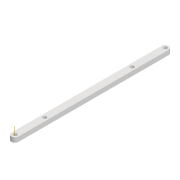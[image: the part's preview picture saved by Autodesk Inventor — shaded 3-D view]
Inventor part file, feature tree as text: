
AUTODESK INVENTOR PART (.ipt)
format: ipt  version: 2022 (Build 260153000, 153)  size: 93,696 bytes
history: native  units: mm
features: extrude x1, other x1, sketch x1
ambient origin geometry x8: Origin, YZ Plane, XZ Plane, XY Plane, X Axis, Y Axis, Z Axis, Center Point
bodies: Solid1 (feature_tree)
feature tree (3):
  extrude  "Extrusion1"  Depth=101.165mm
  other  "Work Axis2"
  sketch  "Sketch1"  dims[d0=3.2mm d1=3.2mm d2=6.0mm d3=129.784mm d4=3.2mm d5=25.613mm d6=4.0mm d7=0.0mm d8=3.2mm d9=101.165mm]
